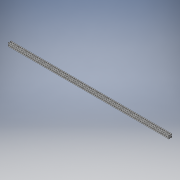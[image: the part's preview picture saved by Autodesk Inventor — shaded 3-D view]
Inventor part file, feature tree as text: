
AUTODESK INVENTOR PART (.ipt)
format: ipt  version: 2019 (Build 230136000, 136)  size: 173,568 bytes
history: native  units: in
note: dims shown in document units (in); Inventor stores cm internally (conversion verified against a paired STEP export)
features: extrude x1, fillet x1, sketch x1
ambient origin geometry x8: Origin, YZ Plane, XZ Plane, XY Plane, X Axis, Y Axis, Z Axis, Center Point
bodies: Solid1 (feature_tree)
feature tree (3):
  extrude  "Extrusion1"  Depth=0.0492in
  fillet  "Fillet1"  [1 undecoded]
  sketch  "Sketch1"  dims[d0=0.1969in d3=0.1417in d4=45.0deg d5=0.122in d7=0.2165in d8=0.063in d11=0.1693in d12=39.3701in d13=0.0in d14=0.0492in]
note: 1 required parameter value undecoded (feature->parameter linkage not recoverable at this tier; creation-order binding heuristic only, values carry confidence <= 0.55)
